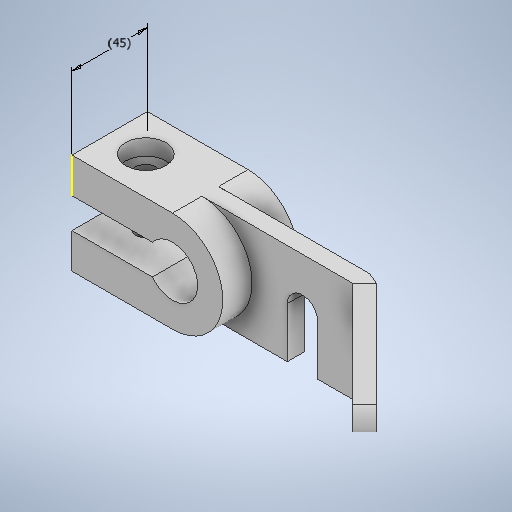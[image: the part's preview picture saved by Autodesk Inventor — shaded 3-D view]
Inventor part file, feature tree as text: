
AUTODESK INVENTOR PART (.ipt)
format: ipt  version: 2025.2 (Build 292293000, 293)  size: 587,776 bytes
history: native  units: in
note: dims shown in document units (in); Inventor stores cm internally (conversion verified against a paired STEP export)
features: sketch x15, extrude x8, plane x3, loft x1, other x1
ambient origin geometry x8: Origin, YZ Plane, XZ Plane, XY Plane, X Axis, Y Axis, Z Axis, Center Point
bodies: Solid1 (feature_tree)
feature tree (28):
  extrude  "Extrusion1"  Depth=2.3622in
  plane  "Work Plane1"
  extrude  "Extrusion2"  TaperAngle=180.0deg  [1 undecoded]
  sketch  "Sketch3"  dims[d14=1.1811in d15=1.1811in]
  sketch  "Sketch4"  dims[d16=0.3937in d17=0.0in d18=135.0deg]
  sketch  "Sketch5"  dims[d19=0.5906in d20=1.7913in]
  plane  "Work Plane2"
  plane  "Work Plane3"
  sketch  "Sketch6"  dims[d21=0.5906in d22=0.2953in d23=0.3937in d24=0.0in]
  sketch  "Sketch7"  dims[d25=1.1811in d26=-1.1811in d27=0.0in d28=90.0deg]
  loft  "Loft1"
  extrude  "Extrusion3"  TaperAngle=135.0deg  [1 undecoded]
  sketch  "Sketch10"  dims[d34=0.7087in]
  extrude  "Extrusion4"  Depth=0.5906in
  extrude  "Extrusion5"  Depth=0.3937in TaperAngle=0.0deg
  extrude  "Extrusion6"  TaperAngle=0.0deg  [1 undecoded]
  extrude  "Extrusion7"  Depth=2.3622in
  extrude  "Extrusion8"  Depth=0.5906in
  sketch  "Sketch1"  dims[d9=3.5433in d10=2.3622in]
  other  "Image1"
  sketch  "Sketch2"  dims[d12=0.3543in d13=180.0deg]
  sketch  "Sketch8"  dims[d29=0.0in d30=90.0deg d31=2.3622in]
  sketch  "Sketch9"  dims[d32=2.3622in d33=0.5906in]
  sketch  "Sketch11"  dims[d35=0.8268in]
  sketch  "Sketch12"  dims[d36=0.689in d37=1.0827in d38=0.0in d39=0.0in]
  sketch  "Sketch13"  dims[d40=1.7717in]
  sketch  "Sketch14"  dims[d42=0.9449in]
  sketch  "Sketch15"  dims[d44=0.374in d45=0.0in d46=0.4724in d47=0.4724in d48=0.0in d49=0.9449in d50=0.3543in d51=0.0in d52=0.4724in d53=0.4724in d54=0.0in d55=0.0in d56=0.0in]
note: 3 required parameter values undecoded (feature->parameter linkage not recoverable at this tier; creation-order binding heuristic only, values carry confidence <= 0.55)
